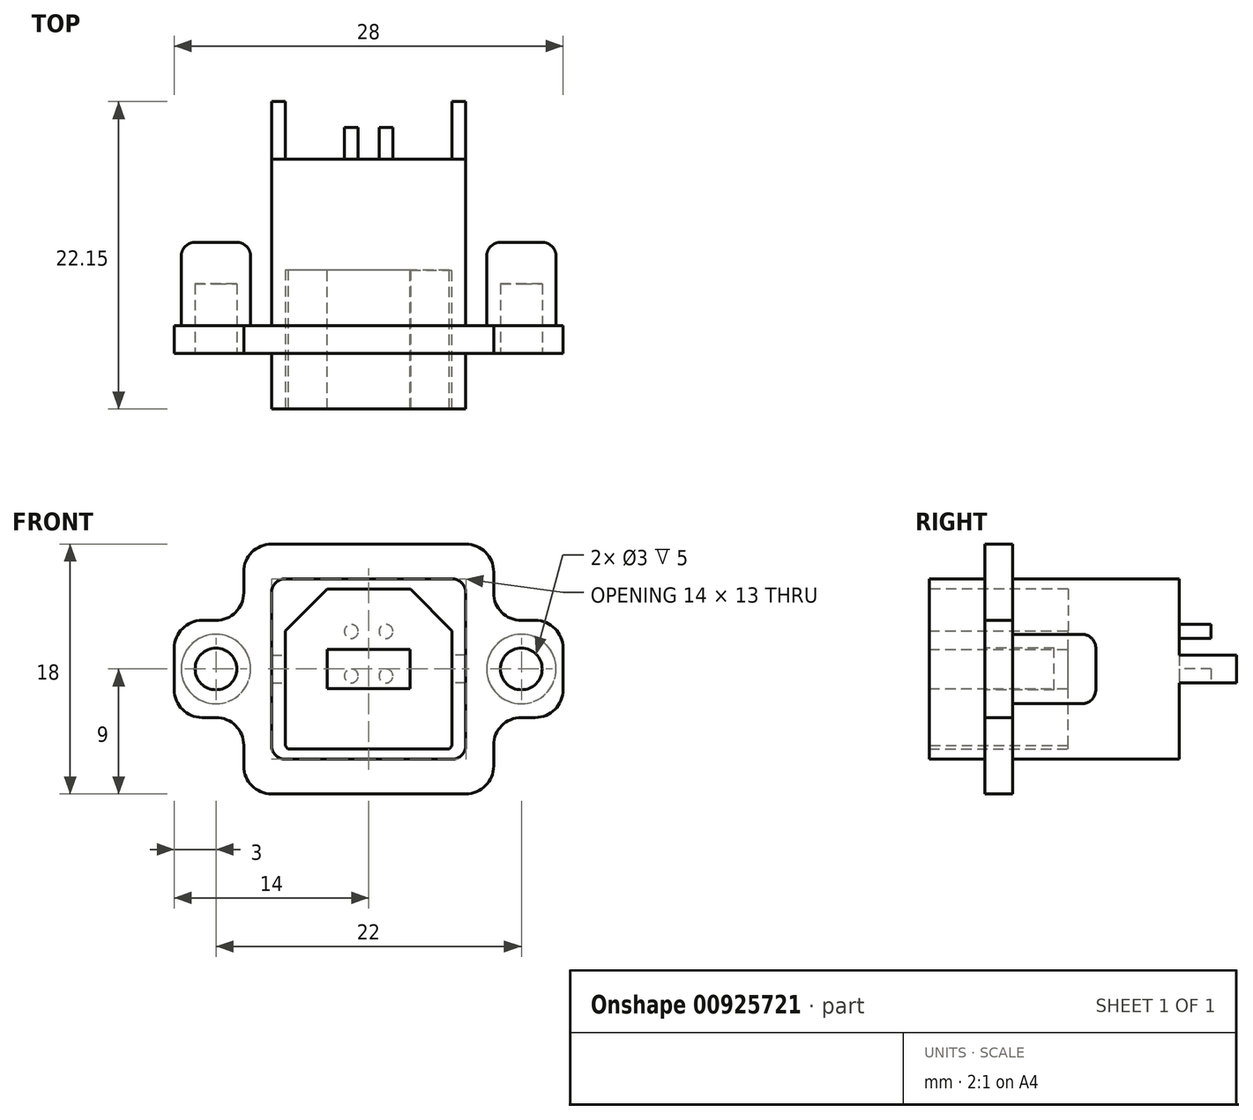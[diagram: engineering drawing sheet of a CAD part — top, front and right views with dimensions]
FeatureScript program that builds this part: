
annotation { "Feature Type Name" : "Feature", "Feature Type Description" : "" }
export const myFeature = defineFeature(function(context is Context, id is Id, definition is map)
    precondition{}
    {
        {
            var Q0;
            Q0=qCreatedBy(makeId("Front.planeOp"),FACE);
            var sketch = newSketch(context, id + "F0", { "sketchPlane" : qUnion([Q0])});
            skLineSegment(sketch, "E0.bottom", {"start": v(9, -9) * mm, "end": v(-9, -9) * mm});
            skLineSegment(sketch, "E0.top", {"start": v(9, 9) * mm, "end": v(-9, 9) * mm});
            skLineSegment(sketch, "E0.left", {"start": v(9, -9) * mm, "end": v(9, 9) * mm});
            skLineSegment(sketch, "E0.right", {"start": v(-9, -9) * mm, "end": v(-9, 9) * mm});
            skPoint(sketch, "E0.middle", {"position": v(0, 0) * mm});
            skLineSegment(sketch, "E1.bottom", {"start": v(-9, 3.5) * mm, "end": v(-14, 3.5) * mm});
            skLineSegment(sketch, "E1.top", {"start": v(-9, -3.5) * mm, "end": v(-14, -3.5) * mm});
            skLineSegment(sketch, "E1.left", {"start": v(-9, 3.5) * mm, "end": v(-9, -3.5) * mm});
            skLineSegment(sketch, "E1.right", {"start": v(-14, 3.5) * mm, "end": v(-14, -3.5) * mm});
            skLineSegment(sketch, "E2.bottom", {"start": v(9, 3.5) * mm, "end": v(14, 3.5) * mm});
            skLineSegment(sketch, "E2.top", {"start": v(9, -3.5) * mm, "end": v(14, -3.5) * mm});
            skLineSegment(sketch, "E2.left", {"start": v(9, 3.5) * mm, "end": v(9, -3.5) * mm});
            skLineSegment(sketch, "E2.right", {"start": v(14, 3.5) * mm, "end": v(14, -3.5) * mm});
            skSolve(sketch);
        }
        {
            var Q0;
            Q0=qSketchRegion(id+"F0",true);
            extrude(context, id + "F1", {"entities" : qUnion([Q0]), "depth" : 2 * mm, "offsetDistance" : 25 * mm});
        }
        {
            var Q0;
            Q0=makeQuery(id+"F1.opExtrude","CAP_FACE",FACE,{"disambiguationData":[OSD([sQuery(id+"F0.wireOp",EDGE,"E0.bottom"),sQuery(id+"F0.wireOp",EDGE,"E0.top"),sQuery(id+"F0.wireOp",EDGE,"E0.left"),sQuery(id+"F0.wireOp",EDGE,"E0.right"),sQuery(id+"F0.wireOp",EDGE,"E1.bottom"),sQuery(id+"F0.wireOp",EDGE,"E1.top"),sQuery(id+"F0.wireOp",EDGE,"E1.right"),sQuery(id+"F0.wireOp",EDGE,"E2.bottom"),sQuery(id+"F0.wireOp",EDGE,"E2.top"),sQuery(id+"F0.wireOp",EDGE,"E2.right")])],"isStart":false});
            var sketch = newSketch(context, id + "F2", { "sketchPlane" : qUnion([Q0])});
            skLineSegment(sketch, "E3.bottom", {"start": v(7, -6.5) * mm, "end": v(-7, -6.5) * mm});
            skLineSegment(sketch, "E3.top", {"start": v(7, 6.5) * mm, "end": v(-7, 6.5) * mm});
            skLineSegment(sketch, "E3.left", {"start": v(7, -6.5) * mm, "end": v(7, 6.5) * mm});
            skLineSegment(sketch, "E3.right", {"start": v(-7, -6.5) * mm, "end": v(-7, 6.5) * mm});
            skPoint(sketch, "E3.middle", {"position": v(0, 0) * mm});
            skSolve(sketch);
        }
        {
            var Q0;
            Q0=qSketchRegion(id+"F2",true);
            extrude(context, id + "F3", {"entities" : qUnion([Q0]), "operationType" : NewBodyOperationType.ADD, "depth" : 4 * mm, "offsetDistance" : 25 * mm});
        }
        {
            var Q0;
            Q0=makeQuery(id+"F1.opExtrude","CAP_FACE",FACE,{"disambiguationData":[OSD([sQuery(id+"F0.wireOp",EDGE,"E0.bottom"),sQuery(id+"F0.wireOp",EDGE,"E0.top"),sQuery(id+"F0.wireOp",EDGE,"E0.left"),sQuery(id+"F0.wireOp",EDGE,"E0.right"),sQuery(id+"F0.wireOp",EDGE,"E1.bottom"),sQuery(id+"F0.wireOp",EDGE,"E1.top"),sQuery(id+"F0.wireOp",EDGE,"E1.right"),sQuery(id+"F0.wireOp",EDGE,"E2.bottom"),sQuery(id+"F0.wireOp",EDGE,"E2.top"),sQuery(id+"F0.wireOp",EDGE,"E2.right")])],"isStart":true});
            var sketch = newSketch(context, id + "F4", { "sketchPlane" : qUnion([Q0])});
            skLineSegment(sketch, "E4.bottom", {"start": v(7, -6.5) * mm, "end": v(-7, -6.5) * mm});
            skLineSegment(sketch, "E4.top", {"start": v(7, 6.5) * mm, "end": v(-7, 6.5) * mm});
            skLineSegment(sketch, "E4.left", {"start": v(7, -6.5) * mm, "end": v(7, 6.5) * mm});
            skLineSegment(sketch, "E4.right", {"start": v(-7, -6.5) * mm, "end": v(-7, 6.5) * mm});
            skPoint(sketch, "E4.middle", {"position": v(0, 0) * mm});
            skSolve(sketch);
        }
        {
            var Q0;
            Q0=qSketchRegion(id+"F4",true);
            extrude(context, id + "F5", {"entities" : qUnion([Q0]), "operationType" : NewBodyOperationType.ADD, "depth" : 12 * mm, "offsetDistance" : 25 * mm});
        }
        {
            var Q0;
            Q0=makeQuery(id+"F1.opExtrude","CAP_FACE",FACE,{"disambiguationData":[OSD([sQuery(id+"F0.wireOp",EDGE,"E0.bottom"),sQuery(id+"F0.wireOp",EDGE,"E0.top"),sQuery(id+"F0.wireOp",EDGE,"E0.left"),sQuery(id+"F0.wireOp",EDGE,"E0.right"),sQuery(id+"F0.wireOp",EDGE,"E1.bottom"),sQuery(id+"F0.wireOp",EDGE,"E1.top"),sQuery(id+"F0.wireOp",EDGE,"E1.right"),sQuery(id+"F0.wireOp",EDGE,"E2.bottom"),sQuery(id+"F0.wireOp",EDGE,"E2.top"),sQuery(id+"F0.wireOp",EDGE,"E2.right")])],"isStart":true});
            var sketch = newSketch(context, id + "F6", { "sketchPlane" : qUnion([Q0])});
            skCircle(sketch, "E5", {"center": v(11, 0) * mm, "radius": 2.5 * mm});
            skCircle(sketch, "E6", {"center": v(-11, 0) * mm, "radius": 2.5 * mm});
            skSolve(sketch);
        }
        {
            var Q0;
            Q0=qSketchRegion(id+"F6",true);
            extrude(context, id + "F7", {"entities" : qUnion([Q0]), "operationType" : NewBodyOperationType.ADD, "depth" : 6 * mm, "offsetDistance" : 25 * mm});
        }
        {
            var Q0;
            Q0=makeQuery(id+"F1.opExtrude","CAP_FACE",FACE,{"disambiguationData":[OSD([sQuery(id+"F0.wireOp",EDGE,"E0.bottom"),sQuery(id+"F0.wireOp",EDGE,"E0.top"),sQuery(id+"F0.wireOp",EDGE,"E0.left"),sQuery(id+"F0.wireOp",EDGE,"E0.right"),sQuery(id+"F0.wireOp",EDGE,"E1.bottom"),sQuery(id+"F0.wireOp",EDGE,"E1.top"),sQuery(id+"F0.wireOp",EDGE,"E1.right"),sQuery(id+"F0.wireOp",EDGE,"E2.bottom"),sQuery(id+"F0.wireOp",EDGE,"E2.top"),sQuery(id+"F0.wireOp",EDGE,"E2.right")])],"isStart":false});
            var sketch = newSketch(context, id + "F8", { "sketchPlane" : qUnion([Q0])});
            skCircle(sketch, "E7", {"center": v(11, 0) * mm, "radius": 1.5 * mm});
            skCircle(sketch, "E8", {"center": v(-11, 0) * mm, "radius": 1.5 * mm});
            skSolve(sketch);
        }
        {
            var Q0;
            Q0=qSketchRegion(id+"F8",true);
            extrude(context, id + "F9", {"entities" : qUnion([Q0]), "operationType" : NewBodyOperationType.REMOVE, "oppositeDirection" : true, "depth" : 5 * mm, "offsetDistance" : 25 * mm});
        }
        {
            var Q0;
            Q0=makeQuery(id+"F1.opExtrude","SWEPT_EDGE",EDGE,{"disambiguationData":[OSD([sQuery(id+"F0.wireOp",EDGE,"E0.top"),sQuery(id+"F0.wireOp",EDGE,"E0.left")])]});
            var Q1;
            Q1=makeQuery(id+"F1.opExtrude","SWEPT_EDGE",EDGE,{"disambiguationData":[OSD([sQuery(id+"F0.wireOp",EDGE,"E0.top"),sQuery(id+"F0.wireOp",EDGE,"E0.right")])]});
            var Q2;
            Q2=makeQuery(id+"F1.opExtrude","SWEPT_EDGE",EDGE,{"disambiguationData":[OSD([sQuery(id+"F0.wireOp",EDGE,"E0.left"),sQuery(id+"F0.wireOp",EDGE,"E2.bottom"),sQuery(id+"F0.wireOp",EDGE,"E2.left")])]});
            var Q3;
            Q3=makeQuery(id+"F1.opExtrude","SWEPT_EDGE",EDGE,{"disambiguationData":[OSD([sQuery(id+"F0.wireOp",EDGE,"E2.bottom"),sQuery(id+"F0.wireOp",EDGE,"E2.right")])]});
            var Q4;
            Q4=makeQuery(id+"F1.opExtrude","SWEPT_EDGE",EDGE,{"disambiguationData":[OSD([sQuery(id+"F0.wireOp",EDGE,"E2.top"),sQuery(id+"F0.wireOp",EDGE,"E2.right")])]});
            var Q5;
            Q5=makeQuery(id+"F1.opExtrude","SWEPT_EDGE",EDGE,{"disambiguationData":[OSD([sQuery(id+"F0.wireOp",EDGE,"E0.left"),sQuery(id+"F0.wireOp",EDGE,"E2.top"),sQuery(id+"F0.wireOp",EDGE,"E2.left")])]});
            var Q6;
            Q6=makeQuery(id+"F1.opExtrude","SWEPT_EDGE",EDGE,{"disambiguationData":[OSD([sQuery(id+"F0.wireOp",EDGE,"E0.bottom"),sQuery(id+"F0.wireOp",EDGE,"E0.left")])]});
            var Q7;
            Q7=makeQuery(id+"F1.opExtrude","SWEPT_EDGE",EDGE,{"disambiguationData":[OSD([sQuery(id+"F0.wireOp",EDGE,"E0.bottom"),sQuery(id+"F0.wireOp",EDGE,"E0.right")])]});
            var Q8;
            Q8=makeQuery(id+"F1.opExtrude","SWEPT_EDGE",EDGE,{"disambiguationData":[OSD([sQuery(id+"F0.wireOp",EDGE,"E0.right"),sQuery(id+"F0.wireOp",EDGE,"E1.top"),sQuery(id+"F0.wireOp",EDGE,"E1.left")])]});
            var Q9;
            Q9=makeQuery(id+"F1.opExtrude","SWEPT_EDGE",EDGE,{"disambiguationData":[OSD([sQuery(id+"F0.wireOp",EDGE,"E1.top"),sQuery(id+"F0.wireOp",EDGE,"E1.right")])]});
            var Q10;
            Q10=makeQuery(id+"F1.opExtrude","SWEPT_EDGE",EDGE,{"disambiguationData":[OSD([sQuery(id+"F0.wireOp",EDGE,"E1.bottom"),sQuery(id+"F0.wireOp",EDGE,"E1.right")])]});
            var Q11;
            Q11=makeQuery(id+"F1.opExtrude","SWEPT_EDGE",EDGE,{"disambiguationData":[OSD([sQuery(id+"F0.wireOp",EDGE,"E0.right"),sQuery(id+"F0.wireOp",EDGE,"E1.bottom"),sQuery(id+"F0.wireOp",EDGE,"E1.left")])]});
            fillet(context, id + "F10", {"entities" : qUnion([Q0, Q1, Q2, Q3, Q4, Q5, Q6, Q7, Q8, Q9, Q10, Q11]), "radius" : 2 * mm, "tangentPropagation" : true, "allowEdgeOverflow" : false});
        }
        {
            var Q0;
            Q0=makeQuery(id+"F3.opExtrude","SWEPT_EDGE",EDGE,{"disambiguationData":[OSD([sQuery(id+"F2.wireOp",EDGE,"E3.top"),sQuery(id+"F2.wireOp",EDGE,"E3.left")])]});
            var Q1;
            Q1=makeQuery(id+"F3.opExtrude","SWEPT_EDGE",EDGE,{"disambiguationData":[OSD([sQuery(id+"F2.wireOp",EDGE,"E3.top"),sQuery(id+"F2.wireOp",EDGE,"E3.right")])]});
            var Q2;
            Q2=makeQuery(id+"F3.opExtrude","SWEPT_EDGE",EDGE,{"disambiguationData":[OSD([sQuery(id+"F2.wireOp",EDGE,"E3.bottom"),sQuery(id+"F2.wireOp",EDGE,"E3.left")])]});
            var Q3;
            Q3=makeQuery(id+"F3.opExtrude","SWEPT_EDGE",EDGE,{"disambiguationData":[OSD([sQuery(id+"F2.wireOp",EDGE,"E3.bottom"),sQuery(id+"F2.wireOp",EDGE,"E3.right")])]});
            var Q4;
            Q4=makeQuery(id+"F5.opExtrude","SWEPT_EDGE",EDGE,{"disambiguationData":[OSD([sQuery(id+"F4.wireOp",EDGE,"E4.top"),sQuery(id+"F4.wireOp",EDGE,"E4.right")])]});
            var Q5;
            Q5=makeQuery(id+"F5.opExtrude","SWEPT_EDGE",EDGE,{"disambiguationData":[OSD([sQuery(id+"F4.wireOp",EDGE,"E4.top"),sQuery(id+"F4.wireOp",EDGE,"E4.left")])]});
            var Q6;
            Q6=makeQuery(id+"F5.opExtrude","SWEPT_EDGE",EDGE,{"disambiguationData":[OSD([sQuery(id+"F4.wireOp",EDGE,"E4.bottom"),sQuery(id+"F4.wireOp",EDGE,"E4.right")])]});
            var Q7;
            Q7=makeQuery(id+"F5.opExtrude","SWEPT_EDGE",EDGE,{"disambiguationData":[OSD([sQuery(id+"F4.wireOp",EDGE,"E4.bottom"),sQuery(id+"F4.wireOp",EDGE,"E4.left")])]});
            fillet(context, id + "F11", {"entities" : qUnion([Q0, Q1, Q2, Q3, Q4, Q5, Q6, Q7]), "radius" : 1 * mm, "tangentPropagation" : true, "allowEdgeOverflow" : false});
        }
        {
            var Q0;
            Q0=makeQuery(id+"F7.opExtrude","CAP_EDGE",EDGE,{"disambiguationData":[OSD([sQuery(id+"F6.wireOp",EDGE,"E6")])],"isStart":false});
            var Q1;
            Q1=makeQuery(id+"F7.opExtrude","CAP_EDGE",EDGE,{"disambiguationData":[OSD([sQuery(id+"F6.wireOp",EDGE,"E5")])],"isStart":false});
            var Q2;
            Q2=makeQuery(id+"F7.opExtrude","CAP_EDGE",EDGE,{"disambiguationData":[OSD([sQuery(id+"F6.wireOp",EDGE,"E6")])],"isStart":true});
            var Q3;
            Q3=makeQuery(id+"F7.opExtrude","CAP_EDGE",EDGE,{"disambiguationData":[OSD([sQuery(id+"F6.wireOp",EDGE,"E5")])],"isStart":true});
            fillet(context, id + "F12", {"entities" : qUnion([Q0, Q1, Q2, Q3]), "radius" : 1 * mm, "tangentPropagation" : true, "allowEdgeOverflow" : false});
        }
        {
            var Q0;
            Q0=makeQuery(id+"F3.opExtrude","CAP_FACE",FACE,{"disambiguationData":[OSD([sQuery(id+"F2.wireOp",EDGE,"E3.bottom"),sQuery(id+"F2.wireOp",EDGE,"E3.top"),sQuery(id+"F2.wireOp",EDGE,"E3.left"),sQuery(id+"F2.wireOp",EDGE,"E3.right")])],"isStart":false});
            var sketch = newSketch(context, id + "F13", { "sketchPlane" : qUnion([Q0])});
            skLineSegment(sketch, "E9.bottom", {"start": v(6, -5.75) * mm, "end": v(-6, -5.75) * mm});
            skLineSegment(sketch, "E9.top", {"start": v(6, 5.75) * mm, "end": v(-6, 5.75) * mm});
            skLineSegment(sketch, "E9.left", {"start": v(6, -5.75) * mm, "end": v(6, 5.75) * mm});
            skLineSegment(sketch, "E9.right", {"start": v(-6, -5.75) * mm, "end": v(-6, 5.75) * mm});
            skPoint(sketch, "E9.middle", {"position": v(0, 0) * mm});
            skSolve(sketch);
        }
        {
            var Q0;
            Q0=qSketchRegion(id+"F13",true);
            extrude(context, id + "F14", {"entities" : qUnion([Q0]), "operationType" : NewBodyOperationType.REMOVE, "oppositeDirection" : true, "depth" : 10 * mm, "offsetDistance" : 25 * mm});
        }
        {
            var Q0;
            Q0=makeQuery(id+"F14.boolean.opBoolean","COPY",EDGE,{"derivedFrom":makeQuery(id+"F14.opExtrude","SWEPT_EDGE",EDGE,{"disambiguationData":[OSD([sQuery(id+"F13.wireOp",EDGE,"E9.bottom"),sQuery(id+"F13.wireOp",EDGE,"E9.left")])]})});
            var Q1;
            Q1=makeQuery(id+"F14.boolean.opBoolean","COPY",EDGE,{"derivedFrom":makeQuery(id+"F14.opExtrude","SWEPT_EDGE",EDGE,{"disambiguationData":[OSD([sQuery(id+"F13.wireOp",EDGE,"E9.bottom"),sQuery(id+"F13.wireOp",EDGE,"E9.right")])]})});
            chamfer(context, id + "F15", {"entities" : qUnion([Q0, Q1]), "width" : 0.2 * mm, "tangentPropagation" : true});
        }
        {
            var Q0;
            Q0=makeQuery(id+"F14.boolean.opBoolean","COPY",EDGE,{"derivedFrom":makeQuery(id+"F14.opExtrude","SWEPT_EDGE",EDGE,{"disambiguationData":[OSD([sQuery(id+"F13.wireOp",EDGE,"E9.top"),sQuery(id+"F13.wireOp",EDGE,"E9.right")])]})});
            var Q1;
            Q1=makeQuery(id+"F14.boolean.opBoolean","COPY",EDGE,{"derivedFrom":makeQuery(id+"F14.opExtrude","SWEPT_EDGE",EDGE,{"disambiguationData":[OSD([sQuery(id+"F13.wireOp",EDGE,"E9.top"),sQuery(id+"F13.wireOp",EDGE,"E9.left")])]})});
            chamfer(context, id + "F16", {"entities" : qUnion([Q0, Q1]), "width" : 3 * mm, "tangentPropagation" : true});
        }
        {
            var Q0;
            Q0=makeQuery(id+"F14.boolean.opBoolean","COPY",FACE,{"derivedFrom":makeQuery(id+"F14.opExtrude","CAP_FACE",FACE,{"disambiguationData":[OSD([sQuery(id+"F13.wireOp",EDGE,"E9.bottom"),sQuery(id+"F13.wireOp",EDGE,"E9.top"),sQuery(id+"F13.wireOp",EDGE,"E9.left"),sQuery(id+"F13.wireOp",EDGE,"E9.right")])],"isStart":false})});
            var sketch = newSketch(context, id + "F17", { "sketchPlane" : qUnion([Q0])});
            skLineSegment(sketch, "E10.bottom", {"start": v(2.97, -1.42) * mm, "end": v(-2.97, -1.42) * mm});
            skLineSegment(sketch, "E10.top", {"start": v(2.97, 1.42) * mm, "end": v(-2.97, 1.42) * mm});
            skLineSegment(sketch, "E10.left", {"start": v(2.97, -1.42) * mm, "end": v(2.97, 1.42) * mm});
            skLineSegment(sketch, "E10.right", {"start": v(-2.97, -1.42) * mm, "end": v(-2.97, 1.42) * mm});
            skPoint(sketch, "E10.middle", {"position": v(0, 0) * mm});
            skSolve(sketch);
        }
        {
            var Q0;
            Q0=qSketchRegion(id+"F17",true);
            extrude(context, id + "F18", {"entities" : qUnion([Q0]), "operationType" : NewBodyOperationType.ADD, "depth" : 10 * mm, "offsetDistance" : 25 * mm});
        }
        {
            var Q0;
            Q0=makeQuery(id+"F5.opExtrude","CAP_FACE",FACE,{"disambiguationData":[OSD([sQuery(id+"F4.wireOp",EDGE,"E4.bottom"),sQuery(id+"F4.wireOp",EDGE,"E4.top"),sQuery(id+"F4.wireOp",EDGE,"E4.left"),sQuery(id+"F4.wireOp",EDGE,"E4.right")])],"isStart":false});
            var sketch = newSketch(context, id + "F19", { "sketchPlane" : qUnion([Q0])});
            skLineSegment(sketch, "E11.bottom", {"start": v(-7, 1) * mm, "end": v(-6, 1) * mm});
            skLineSegment(sketch, "E11.top", {"start": v(-7, -1) * mm, "end": v(-6, -1) * mm});
            skLineSegment(sketch, "E11.left", {"start": v(-7, 1) * mm, "end": v(-7, -1) * mm});
            skLineSegment(sketch, "E11.right", {"start": v(-6, 1) * mm, "end": v(-6, -1) * mm});
            skLineSegment(sketch, "E12.bottom", {"start": v(7, 1) * mm, "end": v(6, 1) * mm});
            skLineSegment(sketch, "E12.top", {"start": v(7, -1) * mm, "end": v(6, -1) * mm});
            skLineSegment(sketch, "E12.left", {"start": v(7, 1) * mm, "end": v(7, -1) * mm});
            skLineSegment(sketch, "E12.right", {"start": v(6, 1) * mm, "end": v(6, -1) * mm});
            skSolve(sketch);
        }
        {
            var Q0;
            Q0=qSketchRegion(id+"F19",true);
            extrude(context, id + "F20", {"entities" : qUnion([Q0]), "operationType" : NewBodyOperationType.ADD, "depth" : 4.15 * mm, "offsetDistance" : 25 * mm});
        }
        {
            var Q0;
            Q0=makeQuery(id+"F5.opExtrude","CAP_FACE",FACE,{"disambiguationData":[OSD([sQuery(id+"F4.wireOp",EDGE,"E4.bottom"),sQuery(id+"F4.wireOp",EDGE,"E4.top"),sQuery(id+"F4.wireOp",EDGE,"E4.left"),sQuery(id+"F4.wireOp",EDGE,"E4.right")])],"isStart":false});
            var sketch = newSketch(context, id + "F21", { "sketchPlane" : qUnion([Q0])});
            skCircle(sketch, "E13", {"center": v(1.25, 2.7) * mm, "radius": 0.5 * mm});
            skCircle(sketch, "E14", {"center": v(-1.25, 2.7) * mm, "radius": 0.5 * mm});
            skCircle(sketch, "E15", {"center": v(1.25, -0.5) * mm, "radius": 0.5 * mm});
            skCircle(sketch, "E16", {"center": v(-1.25, -0.5) * mm, "radius": 0.5 * mm});
            skSolve(sketch);
        }
        {
            var Q0;
            Q0=qSketchRegion(id+"F21",true);
            extrude(context, id + "F22", {"entities" : qUnion([Q0]), "operationType" : NewBodyOperationType.ADD, "depth" : 2.3 * mm, "offsetDistance" : 25 * mm});
        }
    });
